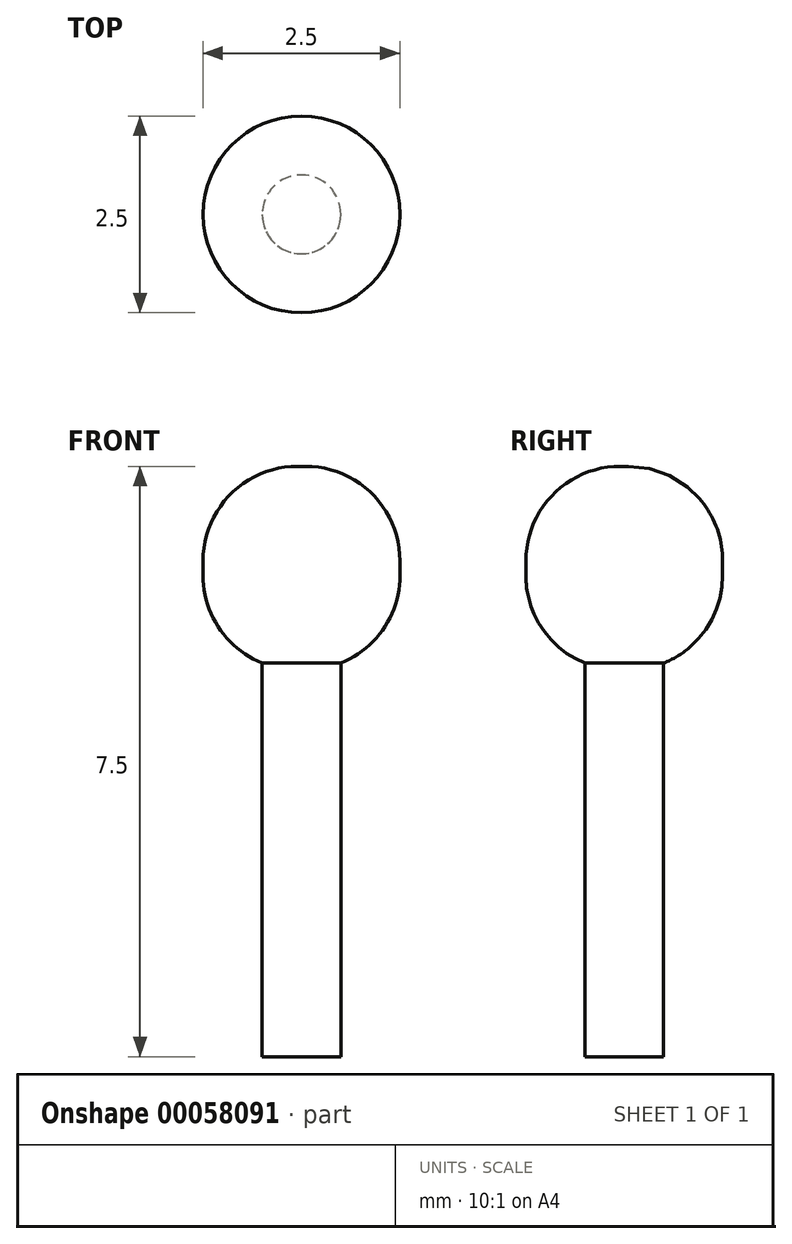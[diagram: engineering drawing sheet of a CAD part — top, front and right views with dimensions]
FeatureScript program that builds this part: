
annotation { "Feature Type Name" : "Feature", "Feature Type Description" : "" }
export const myFeature = defineFeature(function(context is Context, id is Id, definition is map)
    precondition{}
    {
        {
            var Q0;
            Q0=qCreatedBy(makeId("Top.planeOp"),FACE);
            var sketch = newSketch(context, id + "F0", { "sketchPlane" : qUnion([Q0])});
            skCircle(sketch, "E0", {"center": v(0, 0) * mm, "radius": 0.5 * mm});
            skSolve(sketch);
        }
        {
            var Q0;
            Q0=makeQuery(id+"F0.imprint","IMPRINT",FACE,{"disambiguationData":[TD([[makeQuery(id+"F0.imprint","IMPRINT",EDGE,{"derivedFrom":sQuery(id+"F0.wireOp",EDGE,"E0")}),1.0]])]});
            extrude(context, id + "F1", {"entities" : qUnion([Q0]), "depth" : 5 * mm});
        }
        {
            var Q0;
            Q0=makeQuery(id+"F1.opExtrude","CAP_FACE",FACE,{"disambiguationData":[OSD([sQuery(id+"F0.wireOp",EDGE,"E0")])],"isStart":false});
            var sketch = newSketch(context, id + "F2", { "sketchPlane" : qUnion([Q0])});
            skCircle(sketch, "E1", {"center": v(0, 0) * mm, "radius": 1.25 * mm});
            skSolve(sketch);
        }
        {
            var Q0;
            Q0 = qSketchRegion(id + "F2", true);
            extrude(context, id + "F3", {"entities" : qUnion([Q0]), "operationType" : NewBodyOperationType.ADD, "depth" : 2.5 * mm});
        }
        {
            var Q0;
            Q0=makeQuery(id+"F3.opExtrude","CAP_FACE",FACE,{"disambiguationData":[OSD([sQuery(id+"F2.wireOp",EDGE,"E1")])],"isStart":false});
            var Q1;
            Q1=makeQuery(id+"F3.opExtrude","CAP_EDGE",EDGE,{"disambiguationData":[OSD([sQuery(id+"F2.wireOp",EDGE,"E1")])],"isStart":true});
            fillet(context, id + "F4", {"entities" : qUnion([Q0, Q1]), "radius" : 1.2 * mm, "allowEdgeOverflow" : false});
        }
    });
